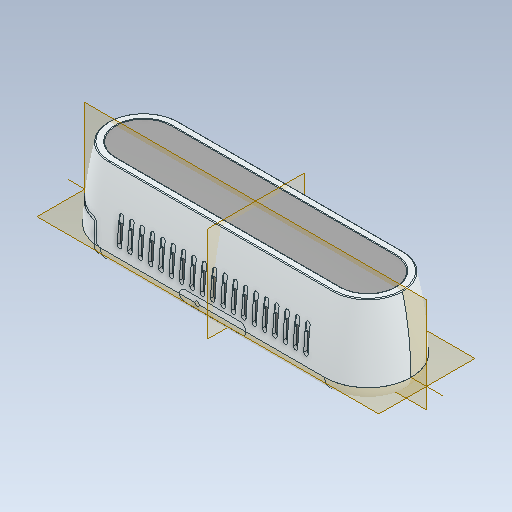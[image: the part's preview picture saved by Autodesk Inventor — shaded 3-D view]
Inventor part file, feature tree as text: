
AUTODESK INVENTOR PART (.ipt)
format: ipt  version: 2021 (Build 250183000, 183)  size: 1,083,392 bytes
history: mixed  units: mm
features: other x4, thread x1, imported_body x1
ambient origin geometry x8: Origin, YZ Plane, XZ Plane, XY Plane, X Axis, Y Axis, Z Axis, Center Point
bodies: Solid1 (imported_parasolid), Solid2 (imported_parasolid), Solid3 (imported_parasolid), Solid4 (imported_parasolid), Solid5 (imported_parasolid)
feature tree (6):
  other  "Split2[2]"
  thread  "Thread1"  [1 undecoded]
  other  "Cut-Extrude10[1]"
  other  "Cut-Extrude10[2]"
  other  "Cut-Extrude12"
  imported_body  NMx_Import_Brep_tag  [imported B-rep: ~21 faces, bbox_mm=None]
note: 1 required parameter value undecoded (feature->parameter linkage not recoverable at this tier; creation-order binding heuristic only, values carry confidence <= 0.55)
